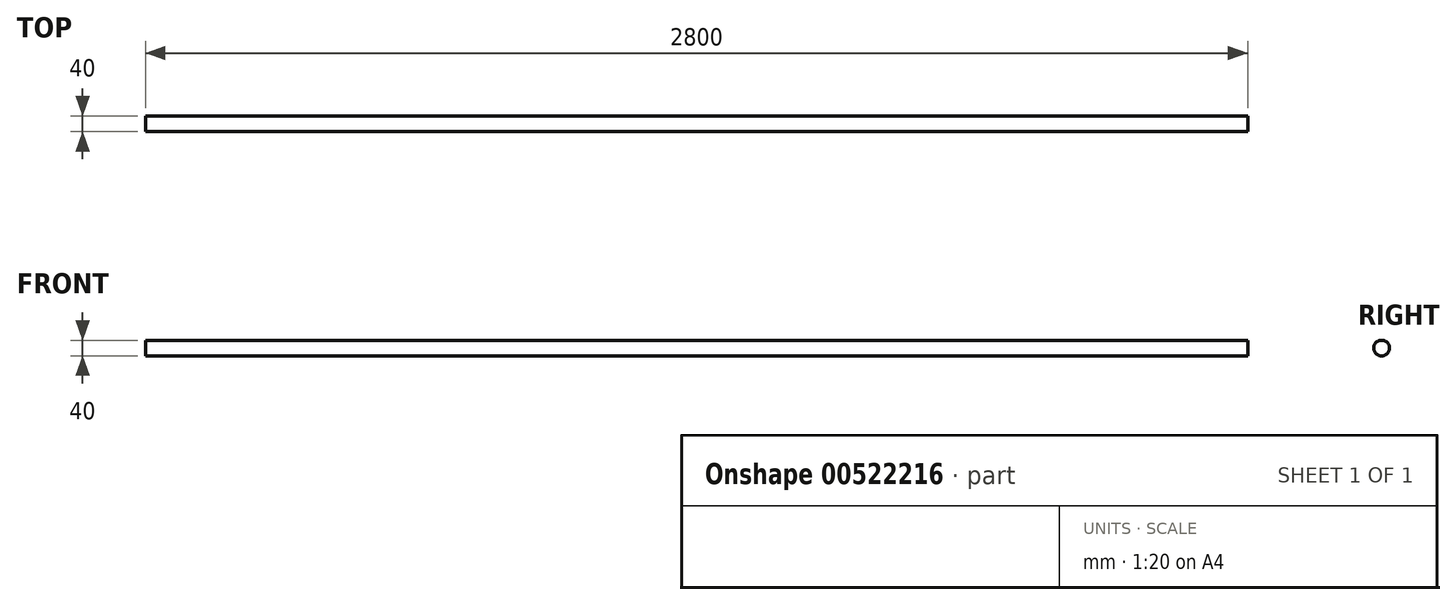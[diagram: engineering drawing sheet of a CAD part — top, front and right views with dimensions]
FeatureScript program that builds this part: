
annotation { "Feature Type Name" : "Feature", "Feature Type Description" : "" }
export const myFeature = defineFeature(function(context is Context, id is Id, definition is map)
    precondition{}
    {
        {
            var Q0;
            Q0=qCreatedBy(makeId("Right.planeOp"),FACE);
            var sketch = newSketch(context, id + "F0", { "sketchPlane" : qUnion([Q0])});
            skCircle(sketch, "E0", {"center": v(0, 0) * mm, "radius": 20 * mm});
            skSolve(sketch);
        }
        {
            var Q0;
            Q0 = qSketchRegion(id + "F0", true);
            extrude(context, id + "F1", {"entities" : qUnion([Q0]), "depth" : 2800 * mm, "offsetDistance" : 25 * mm});
        }
    });
